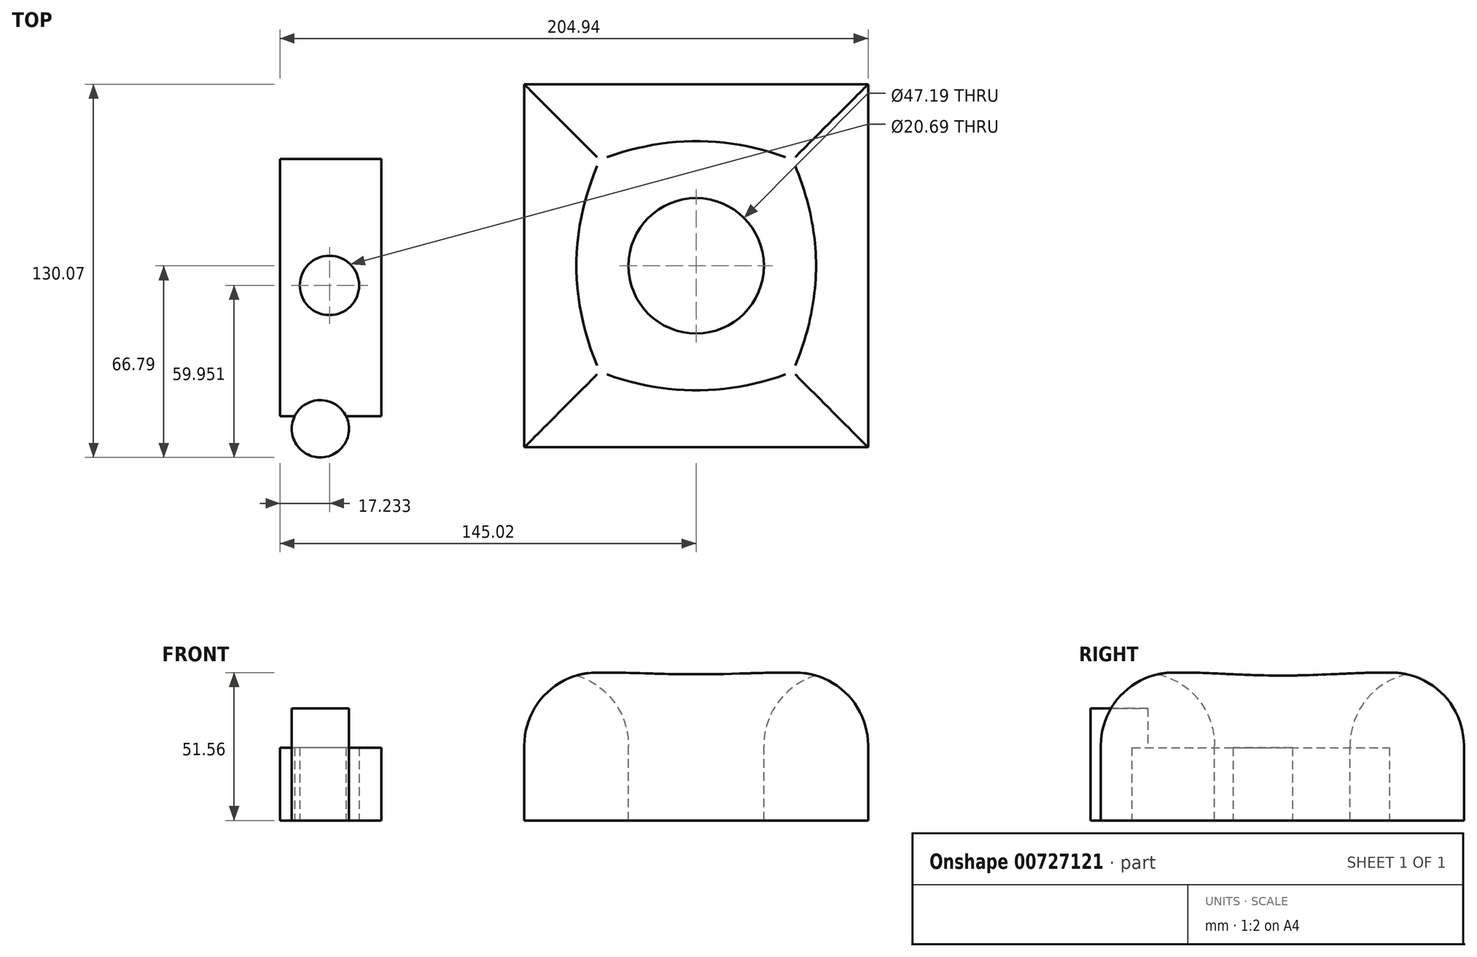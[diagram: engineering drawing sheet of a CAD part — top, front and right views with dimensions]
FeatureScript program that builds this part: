
annotation { "Feature Type Name" : "Feature", "Feature Type Description" : "" }
export const myFeature = defineFeature(function(context is Context, id is Id, definition is map)
    precondition{}
    {
        {
            var Q0;
            Q0=qCreatedBy(makeId("Top.planeOp"),FACE);
            var sketch = newSketch(context, id + "F0", { "sketchPlane" : qUnion([Q0])});
            skLineSegment(sketch, "E0.bottom", {"start": v(59.92, 63.28) * mm, "end": v(-59.92, 63.28) * mm});
            skLineSegment(sketch, "E0.top", {"start": v(59.92, -63.28) * mm, "end": v(-59.92, -63.28) * mm});
            skLineSegment(sketch, "E0.left", {"start": v(59.92, 63.28) * mm, "end": v(59.92, -63.28) * mm});
            skLineSegment(sketch, "E0.right", {"start": v(-59.92, 63.28) * mm, "end": v(-59.92, -63.28) * mm});
            skPoint(sketch, "E0.middle", {"position": v(0, 0) * mm});
            skSolve(sketch);
        }
        {
            var Q0;
            Q0=makeQuery(id+"F0.imprint","IMPRINT",FACE,{"disambiguationData":[TD([[makeQuery(id+"F0.imprint","IMPRINT",EDGE,{"derivedFrom":sQuery(id+"F0.wireOp",EDGE,"E0.bottom")}),1.0]])]});
            extrude(context, id + "F1", {"entities" : qUnion([Q0]), "depth" : 51.56 * mm, "offsetDistance" : 25.4 * mm});
        }
        {
            var Q0;
            Q0=makeQuery(id+"F1.opExtrude","CAP_FACE",FACE,{"disambiguationData":[OSD([sQuery(id+"F0.wireOp",EDGE,"E0.bottom"),sQuery(id+"F0.wireOp",EDGE,"E0.top"),sQuery(id+"F0.wireOp",EDGE,"E0.left"),sQuery(id+"F0.wireOp",EDGE,"E0.right")])],"isStart":false});
            var sketch = newSketch(context, id + "F2", { "sketchPlane" : qUnion([Q0])});
            skCircle(sketch, "E1", {"center": v(0, 0) * mm, "radius": 23.6 * mm});
            skSolve(sketch);
        }
        {
            var Q0;
            Q0=makeQuery(id+"F2.imprint","IMPRINT",FACE,{"disambiguationData":[TD([[makeQuery(id+"F2.imprint","IMPRINT",EDGE,{"derivedFrom":sQuery(id+"F2.wireOp",EDGE,"E1")}),1.0]])]});
            extrude(context, id + "F3", {"entities" : qUnion([Q0]), "operationType" : NewBodyOperationType.REMOVE, "oppositeDirection" : true, "depth" : 115.82 * mm, "offsetDistance" : 25.4 * mm});
        }
        {
            var Q0;
            Q0=makeQuery(id+"F1.opExtrude","CAP_FACE",FACE,{"disambiguationData":[OSD([sQuery(id+"F0.wireOp",EDGE,"E0.bottom"),sQuery(id+"F0.wireOp",EDGE,"E0.top"),sQuery(id+"F0.wireOp",EDGE,"E0.left"),sQuery(id+"F0.wireOp",EDGE,"E0.right")])],"isStart":false});
            fillet(context, id + "F4", {"entities" : qUnion([Q0]), "radius" : 25.4 * mm, "tangentPropagation" : true, "allowEdgeOverflow" : false});
        }
        {
            var Q0;
            Q0=qCreatedBy(makeId("Top.planeOp"),FACE);
            var sketch = newSketch(context, id + "F5", { "sketchPlane" : qUnion([Q0])});
            skLineSegment(sketch, "E2.bottom", {"start": v(-109.7, -52.45) * mm, "end": v(-145.02, -52.45) * mm});
            skLineSegment(sketch, "E2.top", {"start": v(-109.7, 37.3) * mm, "end": v(-145.02, 37.3) * mm});
            skLineSegment(sketch, "E2.left", {"start": v(-109.7, -52.45) * mm, "end": v(-109.7, 37.3) * mm});
            skLineSegment(sketch, "E2.right", {"start": v(-145.02, -52.45) * mm, "end": v(-145.02, 37.3) * mm});
            skCircle(sketch, "E3", {"center": v(-127.79, -6.84) * mm, "radius": 10.34 * mm});
            skSolve(sketch);
        }
        {
            var Q0;
            Q0=makeQuery(id+"F5.imprint","IMPRINT",FACE,{"disambiguationData":[TD([[makeQuery(id+"F5.imprint","IMPRINT",EDGE,{"derivedFrom":sQuery(id+"F5.wireOp",EDGE,"E2.bottom")}),-1.0]])]});
            extrude(context, id + "F6", {"entities" : qUnion([Q0]), "depth" : 25.4 * mm, "offsetDistance" : 25.4 * mm});
        }
        {
            var Q0;
            Q0=qCreatedBy(makeId("Top.planeOp"),FACE);
            var sketch = newSketch(context, id + "F7", { "sketchPlane" : qUnion([Q0])});
            skCircle(sketch, "E4", {"center": v(-130.97, -56.81) * mm, "radius": 9.98 * mm});
            skSolve(sketch);
        }
        {
            var Q0;
            Q0=makeQuery(id+"F7.imprint","IMPRINT",FACE,{"disambiguationData":[TD([[makeQuery(id+"F7.imprint","IMPRINT",EDGE,{"derivedFrom":sQuery(id+"F7.wireOp",EDGE,"E4")}),1.0]])]});
            extrude(context, id + "F8", {"entities" : qUnion([Q0]), "operationType" : NewBodyOperationType.ADD, "depth" : 39.12 * mm, "offsetDistance" : 25.4 * mm});
        }
    });
